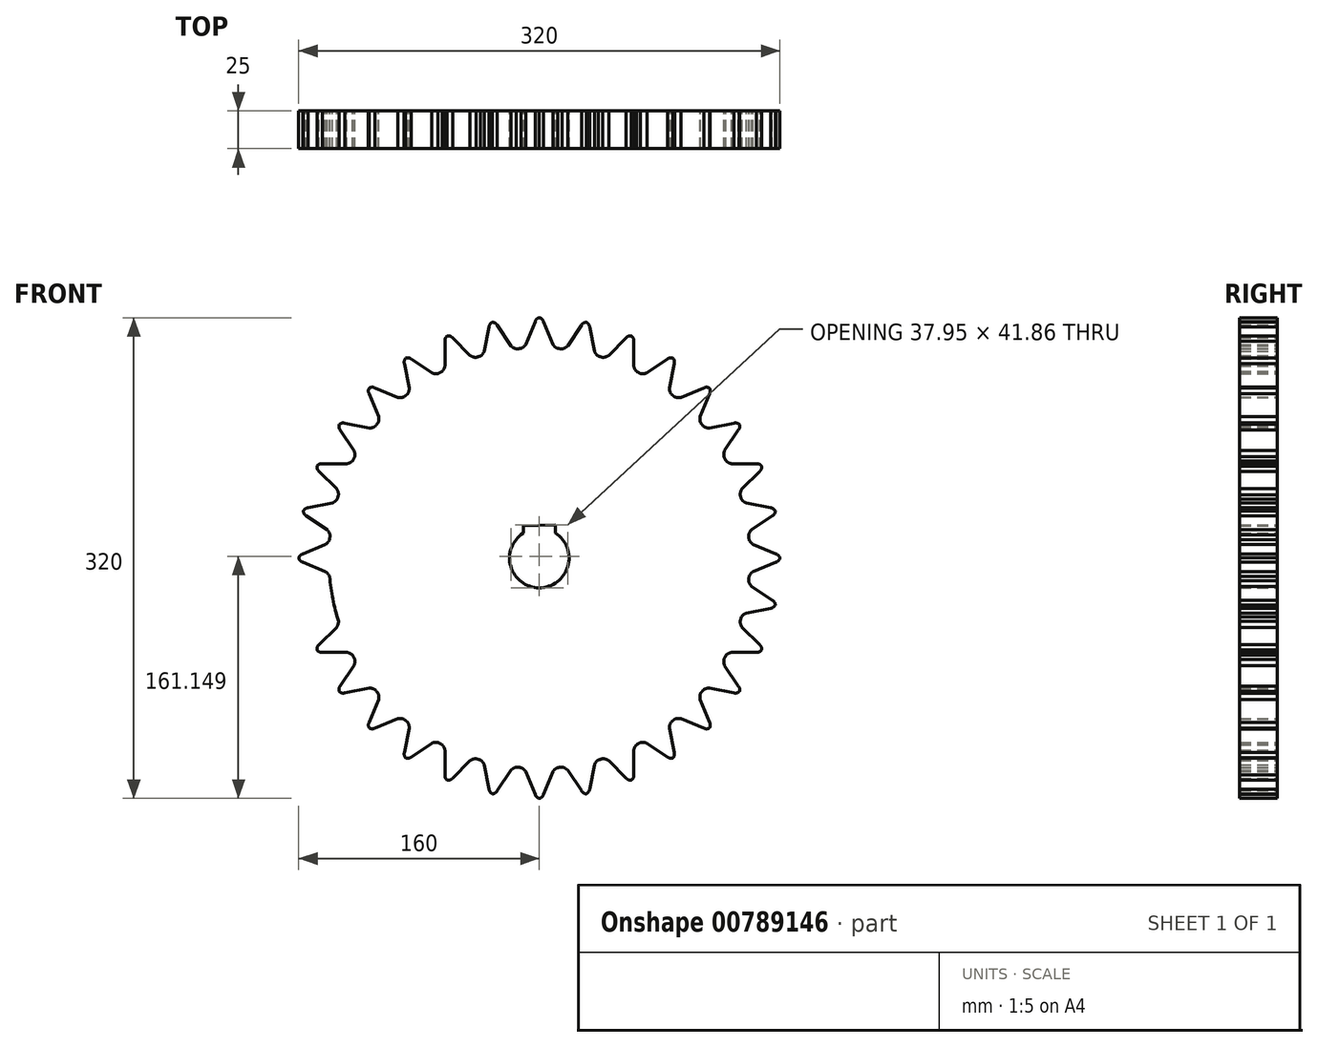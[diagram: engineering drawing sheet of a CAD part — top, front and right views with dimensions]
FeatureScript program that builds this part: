
annotation { "Feature Type Name" : "Feature", "Feature Type Description" : "" }
export const myFeature = defineFeature(function(context is Context, id is Id, definition is map)
    precondition{}
    {
        {
            var Q0;
            Q0=qCreatedBy(makeId("Front.planeOp"),FACE);
            var sketch = newSketch(context, id + "F0", { "sketchPlane" : qUnion([Q0])});
            skArc(sketch, "E0", {"start": v(12.2, 139.47) * mm, "mid": v(0, 140) * mm, "end": v(-12.2, 139.47) * mm});
            skLineSegment(sketch, "E1", {"start": v(0, 0) * mm, "end": v(90.16, 0) * mm});
            skPoint(sketch, "E2.MirrorCS.start.orphan", {"position": v(0, 160) * mm});
            skArc(sketch, "E3", {"start": v(2.75, 157.44) * mm, "mid": v(1.7, 159.07) * mm, "end": v(0, 160) * mm});
            skArc(sketch, "E4", {"start": v(8.99, 142.2) * mm, "mid": v(10.4, 140.61) * mm, "end": v(12.2, 139.47) * mm});
            skLineSegment(sketch, "E5", {"start": v(8.99, 142.2) * mm, "end": v(2.75, 157.44) * mm});
            skArc(sketch, "E6.MirrorCS", {"start": v(-2.75, 157.44) * mm, "mid": v(-1.7, 159.07) * mm, "end": v(0, 160) * mm});
            skLineSegment(sketch, "E7.MirrorCS", {"start": v(-8.99, 142.2) * mm, "end": v(-2.75, 157.44) * mm});
            skArc(sketch, "E8.MirrorCS", {"start": v(-8.99, 142.2) * mm, "mid": v(-10.4, 140.61) * mm, "end": v(-12.2, 139.47) * mm});
            skArc(sketch, "E9.1.0", {"start": v(-36.56, 137.71) * mm, "mid": v(-37.64, 135.88) * mm, "end": v(-39.18, 134.4) * mm});
            skLineSegment(sketch, "E9.1.1", {"start": v(-36.56, 137.71) * mm, "end": v(-33.42, 153.88) * mm});
            skArc(sketch, "E9.1.2", {"start": v(-33.42, 153.88) * mm, "mid": v(-32.7, 155.68) * mm, "end": v(-31.21, 156.93) * mm});
            skArc(sketch, "E9.1.3", {"start": v(-28.01, 154.95) * mm, "mid": v(-29.36, 156.35) * mm, "end": v(-31.21, 156.93) * mm});
            skLineSegment(sketch, "E9.1.4", {"start": v(-18.93, 141.22) * mm, "end": v(-28.01, 154.95) * mm});
            skArc(sketch, "E9.1.5", {"start": v(-18.93, 141.22) * mm, "mid": v(-17.22, 139.94) * mm, "end": v(-15.24, 139.17) * mm});
            skArc(sketch, "E9.2.0", {"start": v(-62.72, 127.94) * mm, "mid": v(-63.43, 125.93) * mm, "end": v(-64.64, 124.18) * mm});
            skLineSegment(sketch, "E9.2.1", {"start": v(-62.72, 127.94) * mm, "end": v(-62.8, 144.4) * mm});
            skArc(sketch, "E9.2.2", {"start": v(-62.8, 144.4) * mm, "mid": v(-62.45, 146.31) * mm, "end": v(-61.23, 147.82) * mm});
            skArc(sketch, "E9.2.3", {"start": v(-57.7, 146.5) * mm, "mid": v(-59.3, 147.62) * mm, "end": v(-61.23, 147.82) * mm});
            skLineSegment(sketch, "E9.2.4", {"start": v(-46.11, 134.81) * mm, "end": v(-57.7, 146.5) * mm});
            skArc(sketch, "E9.2.5", {"start": v(-46.11, 134.81) * mm, "mid": v(-44.2, 133.9) * mm, "end": v(-42.1, 133.52) * mm});
            skArc(sketch, "E9.3.0", {"start": v(-86.47, 113.24) * mm, "mid": v(-86.77, 111.13) * mm, "end": v(-87.63, 109.18) * mm});
            skLineSegment(sketch, "E9.3.1", {"start": v(-86.47, 113.24) * mm, "end": v(-89.76, 129.38) * mm});
            skArc(sketch, "E9.3.2", {"start": v(-89.76, 129.38) * mm, "mid": v(-89.8, 131.32) * mm, "end": v(-88.9, 133.04) * mm});
            skArc(sketch, "E9.3.3", {"start": v(-85.18, 132.44) * mm, "mid": v(-86.96, 133.21) * mm, "end": v(-88.9, 133.04) * mm});
            skLineSegment(sketch, "E9.3.4", {"start": v(-71.53, 123.23) * mm, "end": v(-85.18, 132.44) * mm});
            skArc(sketch, "E9.3.5", {"start": v(-71.53, 123.23) * mm, "mid": v(-69.47, 122.7) * mm, "end": v(-67.34, 122.74) * mm});
            skArc(sketch, "E9.4.0", {"start": v(-106.9, 94.2) * mm, "mid": v(-106.79, 92.07) * mm, "end": v(-107.25, 90) * mm});
            skLineSegment(sketch, "E9.4.1", {"start": v(-106.9, 94.2) * mm, "end": v(-113.27, 109.38) * mm});
            skArc(sketch, "E9.4.2", {"start": v(-113.27, 109.38) * mm, "mid": v(-113.69, 111.28) * mm, "end": v(-113.14, 113.14) * mm});
            skArc(sketch, "E9.4.3", {"start": v(-109.38, 113.27) * mm, "mid": v(-111.28, 113.69) * mm, "end": v(-113.14, 113.14) * mm});
            skLineSegment(sketch, "E9.4.4", {"start": v(-94.2, 106.9) * mm, "end": v(-109.38, 113.27) * mm});
            skArc(sketch, "E9.4.5", {"start": v(-94.2, 106.9) * mm, "mid": v(-92.07, 106.79) * mm, "end": v(-90, 107.25) * mm});
            skArc(sketch, "E9.5.0", {"start": v(-123.23, 71.53) * mm, "mid": v(-122.7, 69.47) * mm, "end": v(-122.74, 67.34) * mm});
            skLineSegment(sketch, "E9.5.1", {"start": v(-123.23, 71.53) * mm, "end": v(-132.44, 85.18) * mm});
            skArc(sketch, "E9.5.2", {"start": v(-132.44, 85.18) * mm, "mid": v(-133.21, 86.96) * mm, "end": v(-133.04, 88.9) * mm});
            skArc(sketch, "E9.5.3", {"start": v(-129.38, 89.76) * mm, "mid": v(-131.32, 89.8) * mm, "end": v(-133.04, 88.9) * mm});
            skLineSegment(sketch, "E9.5.4", {"start": v(-113.24, 86.47) * mm, "end": v(-129.38, 89.76) * mm});
            skArc(sketch, "E9.5.5", {"start": v(-113.24, 86.47) * mm, "mid": v(-111.13, 86.77) * mm, "end": v(-109.18, 87.63) * mm});
            skArc(sketch, "E9.6.0", {"start": v(-134.81, 46.11) * mm, "mid": v(-133.9, 44.2) * mm, "end": v(-133.52, 42.1) * mm});
            skLineSegment(sketch, "E9.6.1", {"start": v(-134.81, 46.11) * mm, "end": v(-146.5, 57.7) * mm});
            skArc(sketch, "E9.6.2", {"start": v(-146.5, 57.7) * mm, "mid": v(-147.62, 59.3) * mm, "end": v(-147.82, 61.23) * mm});
            skArc(sketch, "E9.6.3", {"start": v(-144.4, 62.8) * mm, "mid": v(-146.31, 62.45) * mm, "end": v(-147.82, 61.23) * mm});
            skLineSegment(sketch, "E9.6.4", {"start": v(-127.94, 62.72) * mm, "end": v(-144.4, 62.8) * mm});
            skArc(sketch, "E9.6.5", {"start": v(-127.94, 62.72) * mm, "mid": v(-125.93, 63.43) * mm, "end": v(-124.18, 64.64) * mm});
            skArc(sketch, "E9.7.0", {"start": v(-141.22, 18.93) * mm, "mid": v(-139.94, 17.22) * mm, "end": v(-139.17, 15.24) * mm});
            skLineSegment(sketch, "E9.7.1", {"start": v(-141.22, 18.93) * mm, "end": v(-154.95, 28.01) * mm});
            skArc(sketch, "E9.7.2", {"start": v(-154.95, 28.01) * mm, "mid": v(-156.35, 29.36) * mm, "end": v(-156.93, 31.21) * mm});
            skArc(sketch, "E9.7.3", {"start": v(-153.88, 33.42) * mm, "mid": v(-155.68, 32.7) * mm, "end": v(-156.93, 31.21) * mm});
            skLineSegment(sketch, "E9.7.4", {"start": v(-137.71, 36.56) * mm, "end": v(-153.88, 33.42) * mm});
            skArc(sketch, "E9.7.5", {"start": v(-137.71, 36.56) * mm, "mid": v(-135.88, 37.64) * mm, "end": v(-134.4, 39.18) * mm});
            skArc(sketch, "E9.8.0", {"start": v(-142.2, -8.99) * mm, "mid": v(-140.61, -10.4) * mm, "end": v(-139.47, -12.2) * mm});
            skLineSegment(sketch, "E9.8.1", {"start": v(-142.2, -8.99) * mm, "end": v(-157.44, -2.75) * mm});
            skArc(sketch, "E9.8.2", {"start": v(-157.44, -2.75) * mm, "mid": v(-159.07, -1.7) * mm, "end": v(-160, 0) * mm});
            skArc(sketch, "E9.8.3", {"start": v(-157.44, 2.75) * mm, "mid": v(-159.07, 1.7) * mm, "end": v(-160, 0) * mm});
            skLineSegment(sketch, "E9.8.4", {"start": v(-142.2, 8.99) * mm, "end": v(-157.44, 2.75) * mm});
            skArc(sketch, "E9.8.5", {"start": v(-142.2, 8.99) * mm, "mid": v(-140.61, 10.4) * mm, "end": v(-139.47, 12.2) * mm});
            skArc(sketch, "E9.9.0", {"start": v(-137.71, -36.56) * mm, "mid": v(-135.88, -37.64) * mm, "end": v(-134.4, -39.18) * mm});
            skLineSegment(sketch, "E9.9.1", {"start": v(-137.71, -36.56) * mm, "end": v(-153.88, -33.42) * mm});
            skArc(sketch, "E9.9.2", {"start": v(-153.88, -33.42) * mm, "mid": v(-155.68, -32.7) * mm, "end": v(-156.93, -31.21) * mm});
            skLineSegment(sketch, "E9.9.4", {"start": v(-141.22, -18.93) * mm, "end": v(-154.95, -28.01) * mm});
            skArc(sketch, "E9.9.5", {"start": v(-141.22, -18.93) * mm, "mid": v(-139.94, -17.22) * mm, "end": v(-139.17, -15.24) * mm});
            skArc(sketch, "E9.10.0", {"start": v(-127.94, -62.72) * mm, "mid": v(-125.93, -63.43) * mm, "end": v(-124.18, -64.64) * mm});
            skLineSegment(sketch, "E9.10.1", {"start": v(-127.94, -62.72) * mm, "end": v(-144.4, -62.8) * mm});
            skArc(sketch, "E9.10.2", {"start": v(-144.4, -62.8) * mm, "mid": v(-146.31, -62.45) * mm, "end": v(-147.82, -61.23) * mm});
            skArc(sketch, "E9.10.3", {"start": v(-146.5, -57.7) * mm, "mid": v(-147.62, -59.3) * mm, "end": v(-147.82, -61.23) * mm});
            skLineSegment(sketch, "E9.10.4", {"start": v(-134.81, -46.11) * mm, "end": v(-146.5, -57.7) * mm});
            skArc(sketch, "E9.10.5", {"start": v(-134.81, -46.11) * mm, "mid": v(-133.9, -44.2) * mm, "end": v(-133.52, -42.1) * mm});
            skArc(sketch, "E9.11.0", {"start": v(-113.24, -86.47) * mm, "mid": v(-111.13, -86.77) * mm, "end": v(-109.18, -87.63) * mm});
            skLineSegment(sketch, "E9.11.1", {"start": v(-113.24, -86.47) * mm, "end": v(-129.38, -89.76) * mm});
            skArc(sketch, "E9.11.2", {"start": v(-129.38, -89.76) * mm, "mid": v(-131.32, -89.8) * mm, "end": v(-133.04, -88.9) * mm});
            skArc(sketch, "E9.11.3", {"start": v(-132.44, -85.18) * mm, "mid": v(-133.21, -86.96) * mm, "end": v(-133.04, -88.9) * mm});
            skLineSegment(sketch, "E9.11.4", {"start": v(-123.23, -71.53) * mm, "end": v(-132.44, -85.18) * mm});
            skArc(sketch, "E9.11.5", {"start": v(-123.23, -71.53) * mm, "mid": v(-122.7, -69.47) * mm, "end": v(-122.74, -67.34) * mm});
            skArc(sketch, "E9.12.0", {"start": v(-94.2, -106.9) * mm, "mid": v(-92.07, -106.79) * mm, "end": v(-90, -107.25) * mm});
            skLineSegment(sketch, "E9.12.1", {"start": v(-94.2, -106.9) * mm, "end": v(-109.38, -113.27) * mm});
            skArc(sketch, "E9.12.2", {"start": v(-109.38, -113.27) * mm, "mid": v(-111.28, -113.69) * mm, "end": v(-113.14, -113.14) * mm});
            skArc(sketch, "E9.12.3", {"start": v(-113.27, -109.38) * mm, "mid": v(-113.69, -111.28) * mm, "end": v(-113.14, -113.14) * mm});
            skLineSegment(sketch, "E9.12.4", {"start": v(-106.9, -94.2) * mm, "end": v(-113.27, -109.38) * mm});
            skArc(sketch, "E9.12.5", {"start": v(-106.9, -94.2) * mm, "mid": v(-106.79, -92.07) * mm, "end": v(-107.25, -90) * mm});
            skArc(sketch, "E9.13.0", {"start": v(-71.53, -123.23) * mm, "mid": v(-69.47, -122.7) * mm, "end": v(-67.34, -122.74) * mm});
            skLineSegment(sketch, "E9.13.1", {"start": v(-71.53, -123.23) * mm, "end": v(-85.18, -132.44) * mm});
            skArc(sketch, "E9.13.2", {"start": v(-85.18, -132.44) * mm, "mid": v(-86.96, -133.21) * mm, "end": v(-88.9, -133.04) * mm});
            skArc(sketch, "E9.13.3", {"start": v(-89.76, -129.38) * mm, "mid": v(-89.8, -131.32) * mm, "end": v(-88.9, -133.04) * mm});
            skLineSegment(sketch, "E9.13.4", {"start": v(-86.47, -113.24) * mm, "end": v(-89.76, -129.38) * mm});
            skArc(sketch, "E9.13.5", {"start": v(-86.47, -113.24) * mm, "mid": v(-86.77, -111.13) * mm, "end": v(-87.63, -109.18) * mm});
            skArc(sketch, "E9.14.0", {"start": v(-46.11, -134.81) * mm, "mid": v(-44.2, -133.9) * mm, "end": v(-42.1, -133.52) * mm});
            skLineSegment(sketch, "E9.14.1", {"start": v(-46.11, -134.81) * mm, "end": v(-57.7, -146.5) * mm});
            skArc(sketch, "E9.14.2", {"start": v(-57.7, -146.5) * mm, "mid": v(-59.3, -147.62) * mm, "end": v(-61.23, -147.82) * mm});
            skArc(sketch, "E9.14.3", {"start": v(-62.8, -144.4) * mm, "mid": v(-62.45, -146.31) * mm, "end": v(-61.23, -147.82) * mm});
            skLineSegment(sketch, "E9.14.4", {"start": v(-62.72, -127.94) * mm, "end": v(-62.8, -144.4) * mm});
            skArc(sketch, "E9.14.5", {"start": v(-62.72, -127.94) * mm, "mid": v(-63.43, -125.93) * mm, "end": v(-64.64, -124.18) * mm});
            skArc(sketch, "E9.15.0", {"start": v(-18.93, -141.22) * mm, "mid": v(-17.22, -139.94) * mm, "end": v(-15.24, -139.17) * mm});
            skLineSegment(sketch, "E9.15.1", {"start": v(-18.93, -141.22) * mm, "end": v(-28.01, -154.95) * mm});
            skArc(sketch, "E9.15.2", {"start": v(-28.01, -154.95) * mm, "mid": v(-29.36, -156.35) * mm, "end": v(-31.21, -156.93) * mm});
            skArc(sketch, "E9.15.3", {"start": v(-33.42, -153.88) * mm, "mid": v(-32.7, -155.68) * mm, "end": v(-31.21, -156.93) * mm});
            skLineSegment(sketch, "E9.15.4", {"start": v(-36.56, -137.71) * mm, "end": v(-33.42, -153.88) * mm});
            skArc(sketch, "E9.15.5", {"start": v(-36.56, -137.71) * mm, "mid": v(-37.64, -135.88) * mm, "end": v(-39.18, -134.4) * mm});
            skArc(sketch, "E9.16.0", {"start": v(8.99, -142.2) * mm, "mid": v(10.4, -140.61) * mm, "end": v(12.2, -139.47) * mm});
            skLineSegment(sketch, "E9.16.1", {"start": v(8.99, -142.2) * mm, "end": v(2.75, -157.44) * mm});
            skArc(sketch, "E9.16.2", {"start": v(2.75, -157.44) * mm, "mid": v(1.7, -159.07) * mm, "end": v(0, -160) * mm});
            skArc(sketch, "E9.16.3", {"start": v(-2.75, -157.44) * mm, "mid": v(-1.7, -159.07) * mm, "end": v(0, -160) * mm});
            skLineSegment(sketch, "E9.16.4", {"start": v(-8.99, -142.2) * mm, "end": v(-2.75, -157.44) * mm});
            skArc(sketch, "E9.16.5", {"start": v(-8.99, -142.2) * mm, "mid": v(-10.4, -140.61) * mm, "end": v(-12.2, -139.47) * mm});
            skArc(sketch, "E9.17.0", {"start": v(36.56, -137.71) * mm, "mid": v(37.64, -135.88) * mm, "end": v(39.18, -134.4) * mm});
            skLineSegment(sketch, "E9.17.1", {"start": v(36.56, -137.71) * mm, "end": v(33.42, -153.88) * mm});
            skArc(sketch, "E9.17.2", {"start": v(33.42, -153.88) * mm, "mid": v(32.7, -155.68) * mm, "end": v(31.21, -156.93) * mm});
            skArc(sketch, "E9.17.3", {"start": v(28.01, -154.95) * mm, "mid": v(29.36, -156.35) * mm, "end": v(31.21, -156.93) * mm});
            skLineSegment(sketch, "E9.17.4", {"start": v(18.93, -141.22) * mm, "end": v(28.01, -154.95) * mm});
            skArc(sketch, "E9.17.5", {"start": v(18.93, -141.22) * mm, "mid": v(17.22, -139.94) * mm, "end": v(15.24, -139.17) * mm});
            skArc(sketch, "E9.18.0", {"start": v(62.72, -127.94) * mm, "mid": v(63.43, -125.93) * mm, "end": v(64.64, -124.18) * mm});
            skLineSegment(sketch, "E9.18.1", {"start": v(62.72, -127.94) * mm, "end": v(62.8, -144.4) * mm});
            skArc(sketch, "E9.18.2", {"start": v(62.8, -144.4) * mm, "mid": v(62.45, -146.31) * mm, "end": v(61.23, -147.82) * mm});
            skArc(sketch, "E9.18.3", {"start": v(57.7, -146.5) * mm, "mid": v(59.3, -147.62) * mm, "end": v(61.23, -147.82) * mm});
            skLineSegment(sketch, "E9.18.4", {"start": v(46.11, -134.81) * mm, "end": v(57.7, -146.5) * mm});
            skArc(sketch, "E9.18.5", {"start": v(46.11, -134.81) * mm, "mid": v(44.2, -133.9) * mm, "end": v(42.1, -133.52) * mm});
            skArc(sketch, "E9.19.0", {"start": v(86.47, -113.24) * mm, "mid": v(86.77, -111.13) * mm, "end": v(87.63, -109.18) * mm});
            skLineSegment(sketch, "E9.19.1", {"start": v(86.47, -113.24) * mm, "end": v(89.76, -129.38) * mm});
            skArc(sketch, "E9.19.2", {"start": v(89.76, -129.38) * mm, "mid": v(89.8, -131.32) * mm, "end": v(88.9, -133.04) * mm});
            skArc(sketch, "E9.19.3", {"start": v(85.18, -132.44) * mm, "mid": v(86.96, -133.21) * mm, "end": v(88.9, -133.04) * mm});
            skLineSegment(sketch, "E9.19.4", {"start": v(71.53, -123.23) * mm, "end": v(85.18, -132.44) * mm});
            skArc(sketch, "E9.19.5", {"start": v(71.53, -123.23) * mm, "mid": v(69.47, -122.7) * mm, "end": v(67.34, -122.74) * mm});
            skArc(sketch, "E9.20.0", {"start": v(106.9, -94.2) * mm, "mid": v(106.79, -92.07) * mm, "end": v(107.25, -90) * mm});
            skLineSegment(sketch, "E9.20.1", {"start": v(106.9, -94.2) * mm, "end": v(113.27, -109.38) * mm});
            skArc(sketch, "E9.20.2", {"start": v(113.27, -109.38) * mm, "mid": v(113.69, -111.28) * mm, "end": v(113.14, -113.14) * mm});
            skArc(sketch, "E9.20.3", {"start": v(109.38, -113.27) * mm, "mid": v(111.28, -113.69) * mm, "end": v(113.14, -113.14) * mm});
            skLineSegment(sketch, "E9.20.4", {"start": v(94.2, -106.9) * mm, "end": v(109.38, -113.27) * mm});
            skArc(sketch, "E9.20.5", {"start": v(94.2, -106.9) * mm, "mid": v(92.07, -106.79) * mm, "end": v(90, -107.25) * mm});
            skArc(sketch, "E9.21.0", {"start": v(123.23, -71.53) * mm, "mid": v(122.7, -69.47) * mm, "end": v(122.74, -67.34) * mm});
            skLineSegment(sketch, "E9.21.1", {"start": v(123.23, -71.53) * mm, "end": v(132.44, -85.18) * mm});
            skArc(sketch, "E9.21.2", {"start": v(132.44, -85.18) * mm, "mid": v(133.21, -86.96) * mm, "end": v(133.04, -88.9) * mm});
            skArc(sketch, "E9.21.3", {"start": v(129.38, -89.76) * mm, "mid": v(131.32, -89.8) * mm, "end": v(133.04, -88.9) * mm});
            skLineSegment(sketch, "E9.21.4", {"start": v(113.24, -86.47) * mm, "end": v(129.38, -89.76) * mm});
            skArc(sketch, "E9.21.5", {"start": v(113.24, -86.47) * mm, "mid": v(111.13, -86.77) * mm, "end": v(109.18, -87.63) * mm});
            skArc(sketch, "E9.22.0", {"start": v(134.81, -46.11) * mm, "mid": v(133.9, -44.2) * mm, "end": v(133.52, -42.1) * mm});
            skLineSegment(sketch, "E9.22.1", {"start": v(134.81, -46.11) * mm, "end": v(146.5, -57.7) * mm});
            skArc(sketch, "E9.22.2", {"start": v(146.5, -57.7) * mm, "mid": v(147.62, -59.3) * mm, "end": v(147.82, -61.23) * mm});
            skArc(sketch, "E9.22.3", {"start": v(144.4, -62.8) * mm, "mid": v(146.31, -62.45) * mm, "end": v(147.82, -61.23) * mm});
            skLineSegment(sketch, "E9.22.4", {"start": v(127.94, -62.72) * mm, "end": v(144.4, -62.8) * mm});
            skArc(sketch, "E9.22.5", {"start": v(127.94, -62.72) * mm, "mid": v(125.93, -63.43) * mm, "end": v(124.18, -64.64) * mm});
            skArc(sketch, "E9.23.0", {"start": v(141.22, -18.93) * mm, "mid": v(139.94, -17.22) * mm, "end": v(139.17, -15.24) * mm});
            skLineSegment(sketch, "E9.23.1", {"start": v(141.22, -18.93) * mm, "end": v(154.95, -28.01) * mm});
            skArc(sketch, "E9.23.2", {"start": v(154.95, -28.01) * mm, "mid": v(156.35, -29.36) * mm, "end": v(156.93, -31.21) * mm});
            skArc(sketch, "E9.23.3", {"start": v(153.88, -33.42) * mm, "mid": v(155.68, -32.7) * mm, "end": v(156.93, -31.21) * mm});
            skLineSegment(sketch, "E9.23.4", {"start": v(137.71, -36.56) * mm, "end": v(153.88, -33.42) * mm});
            skArc(sketch, "E9.23.5", {"start": v(137.71, -36.56) * mm, "mid": v(135.88, -37.64) * mm, "end": v(134.4, -39.18) * mm});
            skArc(sketch, "E9.24.0", {"start": v(142.2, 8.99) * mm, "mid": v(140.61, 10.4) * mm, "end": v(139.47, 12.2) * mm});
            skLineSegment(sketch, "E9.24.1", {"start": v(142.2, 8.99) * mm, "end": v(157.44, 2.75) * mm});
            skArc(sketch, "E9.24.2", {"start": v(157.44, 2.75) * mm, "mid": v(159.07, 1.7) * mm, "end": v(160, 0) * mm});
            skArc(sketch, "E9.24.3", {"start": v(157.44, -2.75) * mm, "mid": v(159.07, -1.7) * mm, "end": v(160, 0) * mm});
            skLineSegment(sketch, "E9.24.4", {"start": v(142.2, -8.99) * mm, "end": v(157.44, -2.75) * mm});
            skArc(sketch, "E9.24.5", {"start": v(142.2, -8.99) * mm, "mid": v(140.61, -10.4) * mm, "end": v(139.47, -12.2) * mm});
            skArc(sketch, "E9.25.0", {"start": v(137.71, 36.56) * mm, "mid": v(135.88, 37.64) * mm, "end": v(134.4, 39.18) * mm});
            skLineSegment(sketch, "E9.25.1", {"start": v(137.71, 36.56) * mm, "end": v(153.88, 33.42) * mm});
            skArc(sketch, "E9.25.2", {"start": v(153.88, 33.42) * mm, "mid": v(155.68, 32.7) * mm, "end": v(156.93, 31.21) * mm});
            skArc(sketch, "E9.25.3", {"start": v(154.95, 28.01) * mm, "mid": v(156.35, 29.36) * mm, "end": v(156.93, 31.21) * mm});
            skLineSegment(sketch, "E9.25.4", {"start": v(141.22, 18.93) * mm, "end": v(154.95, 28.01) * mm});
            skArc(sketch, "E9.25.5", {"start": v(141.22, 18.93) * mm, "mid": v(139.94, 17.22) * mm, "end": v(139.17, 15.24) * mm});
            skArc(sketch, "E9.26.0", {"start": v(127.94, 62.72) * mm, "mid": v(125.93, 63.43) * mm, "end": v(124.18, 64.64) * mm});
            skLineSegment(sketch, "E9.26.1", {"start": v(127.94, 62.72) * mm, "end": v(144.4, 62.8) * mm});
            skArc(sketch, "E9.26.2", {"start": v(144.4, 62.8) * mm, "mid": v(146.31, 62.45) * mm, "end": v(147.82, 61.23) * mm});
            skArc(sketch, "E9.26.3", {"start": v(146.5, 57.7) * mm, "mid": v(147.62, 59.3) * mm, "end": v(147.82, 61.23) * mm});
            skLineSegment(sketch, "E9.26.4", {"start": v(134.81, 46.11) * mm, "end": v(146.5, 57.7) * mm});
            skArc(sketch, "E9.26.5", {"start": v(134.81, 46.11) * mm, "mid": v(133.9, 44.2) * mm, "end": v(133.52, 42.1) * mm});
            skArc(sketch, "E9.27.0", {"start": v(113.24, 86.47) * mm, "mid": v(111.13, 86.77) * mm, "end": v(109.18, 87.63) * mm});
            skLineSegment(sketch, "E9.27.1", {"start": v(113.24, 86.47) * mm, "end": v(129.38, 89.76) * mm});
            skArc(sketch, "E9.27.2", {"start": v(129.38, 89.76) * mm, "mid": v(131.32, 89.8) * mm, "end": v(133.04, 88.9) * mm});
            skArc(sketch, "E9.27.3", {"start": v(132.44, 85.18) * mm, "mid": v(133.21, 86.96) * mm, "end": v(133.04, 88.9) * mm});
            skLineSegment(sketch, "E9.27.4", {"start": v(123.23, 71.53) * mm, "end": v(132.44, 85.18) * mm});
            skArc(sketch, "E9.27.5", {"start": v(123.23, 71.53) * mm, "mid": v(122.7, 69.47) * mm, "end": v(122.74, 67.34) * mm});
            skArc(sketch, "E9.28.0", {"start": v(94.2, 106.9) * mm, "mid": v(92.07, 106.79) * mm, "end": v(90, 107.25) * mm});
            skLineSegment(sketch, "E9.28.1", {"start": v(94.2, 106.9) * mm, "end": v(109.38, 113.27) * mm});
            skArc(sketch, "E9.28.2", {"start": v(109.38, 113.27) * mm, "mid": v(111.28, 113.69) * mm, "end": v(113.14, 113.14) * mm});
            skArc(sketch, "E9.28.3", {"start": v(113.27, 109.38) * mm, "mid": v(113.69, 111.28) * mm, "end": v(113.14, 113.14) * mm});
            skLineSegment(sketch, "E9.28.4", {"start": v(106.9, 94.2) * mm, "end": v(113.27, 109.38) * mm});
            skArc(sketch, "E9.28.5", {"start": v(106.9, 94.2) * mm, "mid": v(106.79, 92.07) * mm, "end": v(107.25, 90) * mm});
            skArc(sketch, "E9.29.0", {"start": v(71.53, 123.23) * mm, "mid": v(69.47, 122.7) * mm, "end": v(67.34, 122.74) * mm});
            skLineSegment(sketch, "E9.29.1", {"start": v(71.53, 123.23) * mm, "end": v(85.18, 132.44) * mm});
            skArc(sketch, "E9.29.2", {"start": v(85.18, 132.44) * mm, "mid": v(86.96, 133.21) * mm, "end": v(88.9, 133.04) * mm});
            skArc(sketch, "E9.29.3", {"start": v(89.76, 129.38) * mm, "mid": v(89.8, 131.32) * mm, "end": v(88.9, 133.04) * mm});
            skLineSegment(sketch, "E9.29.4", {"start": v(86.47, 113.24) * mm, "end": v(89.76, 129.38) * mm});
            skArc(sketch, "E9.29.5", {"start": v(86.47, 113.24) * mm, "mid": v(86.77, 111.13) * mm, "end": v(87.63, 109.18) * mm});
            skArc(sketch, "E9.30.0", {"start": v(46.11, 134.81) * mm, "mid": v(44.2, 133.9) * mm, "end": v(42.1, 133.52) * mm});
            skLineSegment(sketch, "E9.30.1", {"start": v(46.11, 134.81) * mm, "end": v(57.7, 146.5) * mm});
            skArc(sketch, "E9.30.2", {"start": v(57.7, 146.5) * mm, "mid": v(59.3, 147.62) * mm, "end": v(61.23, 147.82) * mm});
            skArc(sketch, "E9.30.3", {"start": v(62.8, 144.4) * mm, "mid": v(62.45, 146.31) * mm, "end": v(61.23, 147.82) * mm});
            skLineSegment(sketch, "E9.30.4", {"start": v(62.72, 127.94) * mm, "end": v(62.8, 144.4) * mm});
            skArc(sketch, "E9.30.5", {"start": v(62.72, 127.94) * mm, "mid": v(63.43, 125.93) * mm, "end": v(64.64, 124.18) * mm});
            skArc(sketch, "E9.31.0", {"start": v(18.93, 141.22) * mm, "mid": v(17.22, 139.94) * mm, "end": v(15.24, 139.17) * mm});
            skLineSegment(sketch, "E9.31.1", {"start": v(18.93, 141.22) * mm, "end": v(28.01, 154.95) * mm});
            skArc(sketch, "E9.31.2", {"start": v(28.01, 154.95) * mm, "mid": v(29.36, 156.35) * mm, "end": v(31.21, 156.93) * mm});
            skArc(sketch, "E9.31.3", {"start": v(33.42, 153.88) * mm, "mid": v(32.7, 155.68) * mm, "end": v(31.21, 156.93) * mm});
            skLineSegment(sketch, "E9.31.4", {"start": v(36.56, 137.71) * mm, "end": v(33.42, 153.88) * mm});
            skArc(sketch, "E9.31.5", {"start": v(36.56, 137.71) * mm, "mid": v(37.64, 135.88) * mm, "end": v(39.18, 134.4) * mm});
            skArc(sketch, "E10", {"start": v(-39.18, 134.4) * mm, "mid": v(0, -140) * mm, "end": v(39.18, 134.4) * mm});
            skArc(sketch, "E11.trimOffspring", {"start": v(15.24, 139.17) * mm, "mid": v(0, 140) * mm, "end": v(-15.24, 139.17) * mm});
            skSolve(sketch);
        }
        {
            var Q0;
            Q0 = qSketchRegion(id + "F0", true);
            extrude(context, id + "F1", {"entities" : qUnion([Q0]), "depth" : 25 * mm, "offsetDistance" : 25 * mm});
        }
        {
            var Q0;
            Q0=makeQuery(id+"F1.opExtrude","CAP_FACE",FACE,{"disambiguationData":[OSD([sQuery(id+"F0.wireOp",EDGE,"E3"),sQuery(id+"F0.wireOp",EDGE,"E4"),sQuery(id+"F0.wireOp",EDGE,"E5"),sQuery(id+"F0.wireOp",EDGE,"E6.MirrorCS"),sQuery(id+"F0.wireOp",EDGE,"E7.MirrorCS"),sQuery(id+"F0.wireOp",EDGE,"E8.MirrorCS"),sQuery(id+"F0.wireOp",EDGE,"E9.1.0"),sQuery(id+"F0.wireOp",EDGE,"E9.1.1"),sQuery(id+"F0.wireOp",EDGE,"E9.1.2"),sQuery(id+"F0.wireOp",EDGE,"E9.1.3"),sQuery(id+"F0.wireOp",EDGE,"E9.1.4"),sQuery(id+"F0.wireOp",EDGE,"E9.1.5"),sQuery(id+"F0.wireOp",EDGE,"E9.2.0"),sQuery(id+"F0.wireOp",EDGE,"E9.2.1"),sQuery(id+"F0.wireOp",EDGE,"E9.2.2"),sQuery(id+"F0.wireOp",EDGE,"E9.2.3"),sQuery(id+"F0.wireOp",EDGE,"E9.2.4"),sQuery(id+"F0.wireOp",EDGE,"E9.2.5"),sQuery(id+"F0.wireOp",EDGE,"E9.3.0"),sQuery(id+"F0.wireOp",EDGE,"E9.3.1"),sQuery(id+"F0.wireOp",EDGE,"E9.3.2"),sQuery(id+"F0.wireOp",EDGE,"E9.3.3"),sQuery(id+"F0.wireOp",EDGE,"E9.3.4"),sQuery(id+"F0.wireOp",EDGE,"E9.3.5"),sQuery(id+"F0.wireOp",EDGE,"E9.4.0"),sQuery(id+"F0.wireOp",EDGE,"E9.4.1"),sQuery(id+"F0.wireOp",EDGE,"E9.4.2"),sQuery(id+"F0.wireOp",EDGE,"E9.4.3"),sQuery(id+"F0.wireOp",EDGE,"E9.4.4"),sQuery(id+"F0.wireOp",EDGE,"E9.4.5"),sQuery(id+"F0.wireOp",EDGE,"E9.5.0"),sQuery(id+"F0.wireOp",EDGE,"E9.5.1"),sQuery(id+"F0.wireOp",EDGE,"E9.5.2"),sQuery(id+"F0.wireOp",EDGE,"E9.5.3"),sQuery(id+"F0.wireOp",EDGE,"E9.5.4"),sQuery(id+"F0.wireOp",EDGE,"E9.5.5"),sQuery(id+"F0.wireOp",EDGE,"E9.6.0"),sQuery(id+"F0.wireOp",EDGE,"E9.6.1"),sQuery(id+"F0.wireOp",EDGE,"E9.6.2"),sQuery(id+"F0.wireOp",EDGE,"E9.6.3"),sQuery(id+"F0.wireOp",EDGE,"E9.6.4"),sQuery(id+"F0.wireOp",EDGE,"E9.6.5"),sQuery(id+"F0.wireOp",EDGE,"E9.7.0"),sQuery(id+"F0.wireOp",EDGE,"E9.7.1"),sQuery(id+"F0.wireOp",EDGE,"E9.7.2"),sQuery(id+"F0.wireOp",EDGE,"E9.7.3"),sQuery(id+"F0.wireOp",EDGE,"E9.7.4"),sQuery(id+"F0.wireOp",EDGE,"E9.7.5"),sQuery(id+"F0.wireOp",EDGE,"E9.8.0"),sQuery(id+"F0.wireOp",EDGE,"E9.8.1"),sQuery(id+"F0.wireOp",EDGE,"E9.8.2"),sQuery(id+"F0.wireOp",EDGE,"E9.8.3"),sQuery(id+"F0.wireOp",EDGE,"E9.8.4"),sQuery(id+"F0.wireOp",EDGE,"E9.8.5"),sQuery(id+"F0.wireOp",EDGE,"E9.10.0"),sQuery(id+"F0.wireOp",EDGE,"E9.10.1"),sQuery(id+"F0.wireOp",EDGE,"E9.10.2"),sQuery(id+"F0.wireOp",EDGE,"E9.10.3"),sQuery(id+"F0.wireOp",EDGE,"E9.10.4"),sQuery(id+"F0.wireOp",EDGE,"E9.10.5"),sQuery(id+"F0.wireOp",EDGE,"E9.11.0"),sQuery(id+"F0.wireOp",EDGE,"E9.11.1"),sQuery(id+"F0.wireOp",EDGE,"E9.11.2"),sQuery(id+"F0.wireOp",EDGE,"E9.11.3"),sQuery(id+"F0.wireOp",EDGE,"E9.11.4"),sQuery(id+"F0.wireOp",EDGE,"E9.11.5"),sQuery(id+"F0.wireOp",EDGE,"E9.12.0"),sQuery(id+"F0.wireOp",EDGE,"E9.12.1"),sQuery(id+"F0.wireOp",EDGE,"E9.12.2"),sQuery(id+"F0.wireOp",EDGE,"E9.12.3"),sQuery(id+"F0.wireOp",EDGE,"E9.12.4"),sQuery(id+"F0.wireOp",EDGE,"E9.12.5"),sQuery(id+"F0.wireOp",EDGE,"E9.13.0"),sQuery(id+"F0.wireOp",EDGE,"E9.13.1"),sQuery(id+"F0.wireOp",EDGE,"E9.13.2"),sQuery(id+"F0.wireOp",EDGE,"E9.13.3"),sQuery(id+"F0.wireOp",EDGE,"E9.13.4"),sQuery(id+"F0.wireOp",EDGE,"E9.13.5"),sQuery(id+"F0.wireOp",EDGE,"E9.14.0"),sQuery(id+"F0.wireOp",EDGE,"E9.14.1"),sQuery(id+"F0.wireOp",EDGE,"E9.14.2"),sQuery(id+"F0.wireOp",EDGE,"E9.14.3"),sQuery(id+"F0.wireOp",EDGE,"E9.14.4"),sQuery(id+"F0.wireOp",EDGE,"E9.14.5"),sQuery(id+"F0.wireOp",EDGE,"E9.15.0"),sQuery(id+"F0.wireOp",EDGE,"E9.15.1"),sQuery(id+"F0.wireOp",EDGE,"E9.15.2"),sQuery(id+"F0.wireOp",EDGE,"E9.15.3"),sQuery(id+"F0.wireOp",EDGE,"E9.15.4"),sQuery(id+"F0.wireOp",EDGE,"E9.15.5"),sQuery(id+"F0.wireOp",EDGE,"E9.16.0"),sQuery(id+"F0.wireOp",EDGE,"E9.16.1"),sQuery(id+"F0.wireOp",EDGE,"E9.16.2"),sQuery(id+"F0.wireOp",EDGE,"E9.16.3"),sQuery(id+"F0.wireOp",EDGE,"E9.16.4"),sQuery(id+"F0.wireOp",EDGE,"E9.16.5"),sQuery(id+"F0.wireOp",EDGE,"E9.17.0"),sQuery(id+"F0.wireOp",EDGE,"E9.17.1"),sQuery(id+"F0.wireOp",EDGE,"E9.17.2"),sQuery(id+"F0.wireOp",EDGE,"E9.17.3"),sQuery(id+"F0.wireOp",EDGE,"E9.17.4"),sQuery(id+"F0.wireOp",EDGE,"E9.17.5"),sQuery(id+"F0.wireOp",EDGE,"E9.18.0"),sQuery(id+"F0.wireOp",EDGE,"E9.18.1"),sQuery(id+"F0.wireOp",EDGE,"E9.18.2"),sQuery(id+"F0.wireOp",EDGE,"E9.18.3"),sQuery(id+"F0.wireOp",EDGE,"E9.18.4"),sQuery(id+"F0.wireOp",EDGE,"E9.18.5"),sQuery(id+"F0.wireOp",EDGE,"E9.19.0"),sQuery(id+"F0.wireOp",EDGE,"E9.19.1"),sQuery(id+"F0.wireOp",EDGE,"E9.19.2"),sQuery(id+"F0.wireOp",EDGE,"E9.19.3"),sQuery(id+"F0.wireOp",EDGE,"E9.19.4"),sQuery(id+"F0.wireOp",EDGE,"E9.19.5"),sQuery(id+"F0.wireOp",EDGE,"E9.20.0"),sQuery(id+"F0.wireOp",EDGE,"E9.20.1"),sQuery(id+"F0.wireOp",EDGE,"E9.20.2"),sQuery(id+"F0.wireOp",EDGE,"E9.20.3"),sQuery(id+"F0.wireOp",EDGE,"E9.20.4"),sQuery(id+"F0.wireOp",EDGE,"E9.20.5"),sQuery(id+"F0.wireOp",EDGE,"E9.21.0"),sQuery(id+"F0.wireOp",EDGE,"E9.21.1"),sQuery(id+"F0.wireOp",EDGE,"E9.21.2"),sQuery(id+"F0.wireOp",EDGE,"E9.21.3"),sQuery(id+"F0.wireOp",EDGE,"E9.21.4"),sQuery(id+"F0.wireOp",EDGE,"E9.21.5"),sQuery(id+"F0.wireOp",EDGE,"E9.22.0"),sQuery(id+"F0.wireOp",EDGE,"E9.22.1"),sQuery(id+"F0.wireOp",EDGE,"E9.22.2"),sQuery(id+"F0.wireOp",EDGE,"E9.22.3"),sQuery(id+"F0.wireOp",EDGE,"E9.22.4"),sQuery(id+"F0.wireOp",EDGE,"E9.22.5"),sQuery(id+"F0.wireOp",EDGE,"E9.23.0"),sQuery(id+"F0.wireOp",EDGE,"E9.23.1"),sQuery(id+"F0.wireOp",EDGE,"E9.23.2"),sQuery(id+"F0.wireOp",EDGE,"E9.23.3"),sQuery(id+"F0.wireOp",EDGE,"E9.23.4"),sQuery(id+"F0.wireOp",EDGE,"E9.23.5"),sQuery(id+"F0.wireOp",EDGE,"E9.24.0"),sQuery(id+"F0.wireOp",EDGE,"E9.24.1"),sQuery(id+"F0.wireOp",EDGE,"E9.24.2"),sQuery(id+"F0.wireOp",EDGE,"E9.24.3"),sQuery(id+"F0.wireOp",EDGE,"E9.24.4"),sQuery(id+"F0.wireOp",EDGE,"E9.24.5"),sQuery(id+"F0.wireOp",EDGE,"E9.25.0"),sQuery(id+"F0.wireOp",EDGE,"E9.25.1"),sQuery(id+"F0.wireOp",EDGE,"E9.25.2"),sQuery(id+"F0.wireOp",EDGE,"E9.25.3"),sQuery(id+"F0.wireOp",EDGE,"E9.25.4"),sQuery(id+"F0.wireOp",EDGE,"E9.25.5"),sQuery(id+"F0.wireOp",EDGE,"E9.26.0"),sQuery(id+"F0.wireOp",EDGE,"E9.26.1"),sQuery(id+"F0.wireOp",EDGE,"E9.26.2"),sQuery(id+"F0.wireOp",EDGE,"E9.26.3"),sQuery(id+"F0.wireOp",EDGE,"E9.26.4"),sQuery(id+"F0.wireOp",EDGE,"E9.26.5"),sQuery(id+"F0.wireOp",EDGE,"E9.27.0"),sQuery(id+"F0.wireOp",EDGE,"E9.27.1"),sQuery(id+"F0.wireOp",EDGE,"E9.27.2"),sQuery(id+"F0.wireOp",EDGE,"E9.27.3"),sQuery(id+"F0.wireOp",EDGE,"E9.27.4"),sQuery(id+"F0.wireOp",EDGE,"E9.27.5"),sQuery(id+"F0.wireOp",EDGE,"E9.28.0"),sQuery(id+"F0.wireOp",EDGE,"E9.28.1"),sQuery(id+"F0.wireOp",EDGE,"E9.28.2"),sQuery(id+"F0.wireOp",EDGE,"E9.28.3"),sQuery(id+"F0.wireOp",EDGE,"E9.28.4"),sQuery(id+"F0.wireOp",EDGE,"E9.28.5"),sQuery(id+"F0.wireOp",EDGE,"E9.29.0"),sQuery(id+"F0.wireOp",EDGE,"E9.29.1"),sQuery(id+"F0.wireOp",EDGE,"E9.29.2"),sQuery(id+"F0.wireOp",EDGE,"E9.29.3"),sQuery(id+"F0.wireOp",EDGE,"E9.29.4"),sQuery(id+"F0.wireOp",EDGE,"E9.29.5"),sQuery(id+"F0.wireOp",EDGE,"E9.30.0"),sQuery(id+"F0.wireOp",EDGE,"E9.30.1"),sQuery(id+"F0.wireOp",EDGE,"E9.30.2"),sQuery(id+"F0.wireOp",EDGE,"E9.30.3"),sQuery(id+"F0.wireOp",EDGE,"E9.30.4"),sQuery(id+"F0.wireOp",EDGE,"E9.30.5"),sQuery(id+"F0.wireOp",EDGE,"E9.31.0"),sQuery(id+"F0.wireOp",EDGE,"E9.31.1"),sQuery(id+"F0.wireOp",EDGE,"E9.31.2"),sQuery(id+"F0.wireOp",EDGE,"E9.31.3"),sQuery(id+"F0.wireOp",EDGE,"E9.31.4"),sQuery(id+"F0.wireOp",EDGE,"E9.31.5"),sQuery(id+"F0.wireOp",EDGE,"E10"),sQuery(id+"F0.wireOp",EDGE,"E11.trimOffspring")])],"isStart":true});
            var sketch = newSketch(context, id + "F2", { "sketchPlane" : qUnion([Q0])});
            skArc(sketch, "E12", {"start": v(-10.7, 16.64) * mm, "mid": v(0, -19.78) * mm, "end": v(10.7, 16.64) * mm});
            skLineSegment(sketch, "E13", {"start": v(10.7, 16.64) * mm, "end": v(10.7, 21.4) * mm});
            skPoint(sketch, "E14.end.orphan", {"position": v(-10.7, 11.37) * mm});
            skPoint(sketch, "E15.end.orphan", {"position": v(10.7, 11.37) * mm});
            skPoint(sketch, "E16.start.orphan", {"position": v(-10.7, 22.08) * mm});
            skLineSegment(sketch, "E17", {"start": v(-10.7, 16.64) * mm, "end": v(-10.7, 22.08) * mm});
            skLineSegment(sketch, "E18", {"start": v(10.7, 21.4) * mm, "end": v(-10.7, 22.08) * mm});
            skSolve(sketch);
        }
        {
            var Q0;
            Q0=makeQuery(id+"F2.imprint","IMPRINT",FACE,{"disambiguationData":[TD([[makeQuery(id+"F2.imprint","IMPRINT",EDGE,{"derivedFrom":sQuery(id+"F2.wireOp",EDGE,"E12")}),1.0]])]});
            extrude(context, id + "F3", {"entities" : qUnion([Q0]), "operationType" : NewBodyOperationType.REMOVE, "oppositeDirection" : true, "depth" : 25 * mm, "offsetDistance" : 25 * mm});
        }
    });
